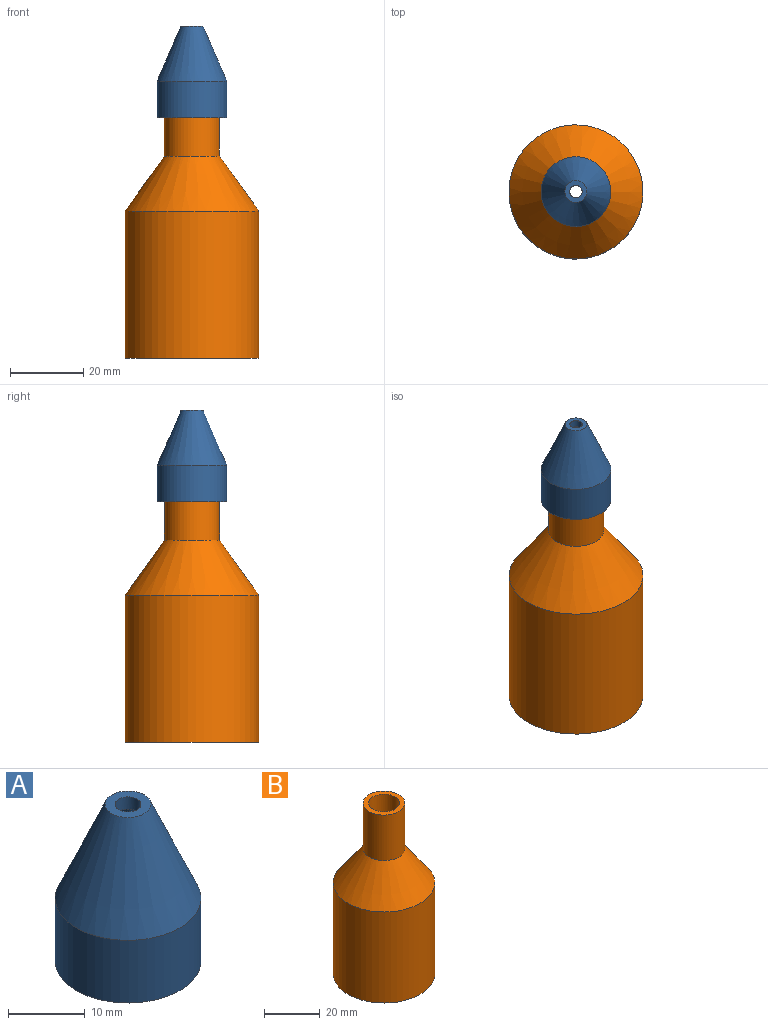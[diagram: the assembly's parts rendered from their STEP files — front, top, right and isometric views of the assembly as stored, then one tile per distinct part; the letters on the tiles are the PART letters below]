
ASSEMBLY  parts=2 mates=1
PART A: 7 faces, bbox 19x19x25 mm
  f0: cylinder r=7.5mm len=15mm, axis (0,0,1), area 451.7mm2, adj f1,f5
  f1: plane 19x19mm, normal (0,0,-1), area 106.8mm2, adj f0,f2
  f2: cylinder r=9.5mm len=19mm, axis (0,0,1), area 596.9mm2, adj f1,f3
  f3: cone r=9.5mm half-angle=23.4deg, axis (0,0,-1), area 642mm2, adj f2,f4
  f4: plane 6x6mm, normal (0,0,1), area 19.3mm2, adj f3,f6
  f5: cone r=1.69mm half-angle=23.4deg, axis (0,0,-1), area 422mm2, adj f0,f6
  f6: cylinder r=1.69mm len=3.37mm, axis (0,0,-1), area 21.2mm2, adj f4,f5
PART B: 8 faces, bbox 36.5x36.5x75 mm
  f0: cylinder r=15.25mm len=39.04mm, axis (0,0,1), area 3740.4mm2, adj f1,f5
  f1: plane 36.5x36.5mm, normal (0,0,-1), area 315.7mm2, adj f0,f2
  f2: cylinder r=18.25mm len=40mm, axis (0,0,1), area 4586.7mm2, adj f1,f3
  f3: cone r=18.25mm half-angle=35.6deg, axis (0,0,-1), area 1492.9mm2, adj f2,f4
  f4: cylinder r=7.5mm len=20mm, axis (0,0,1), area 942.5mm2, adj f3,f7
  f5: cone r=4.5mm half-angle=35.6deg, axis (0,0,-1), area 1091.1mm2, adj f0,f6
  f6: cylinder r=5.5mm len=22.36mm, axis (0,0,1), area 772.7mm2, adj f5,f7
  f7: plane 15x15mm, normal (0,0,1), area 81.7mm2, adj f4,f6
PLACE A t=(-51.97,-37.01,17.41)mm
PLACE B t=(-51.97,-37.01,-48)mm
MATE fastened A.f3 <-> B.f6  axis (0,0,-1) through (-51.97,-37.01,27)mm
